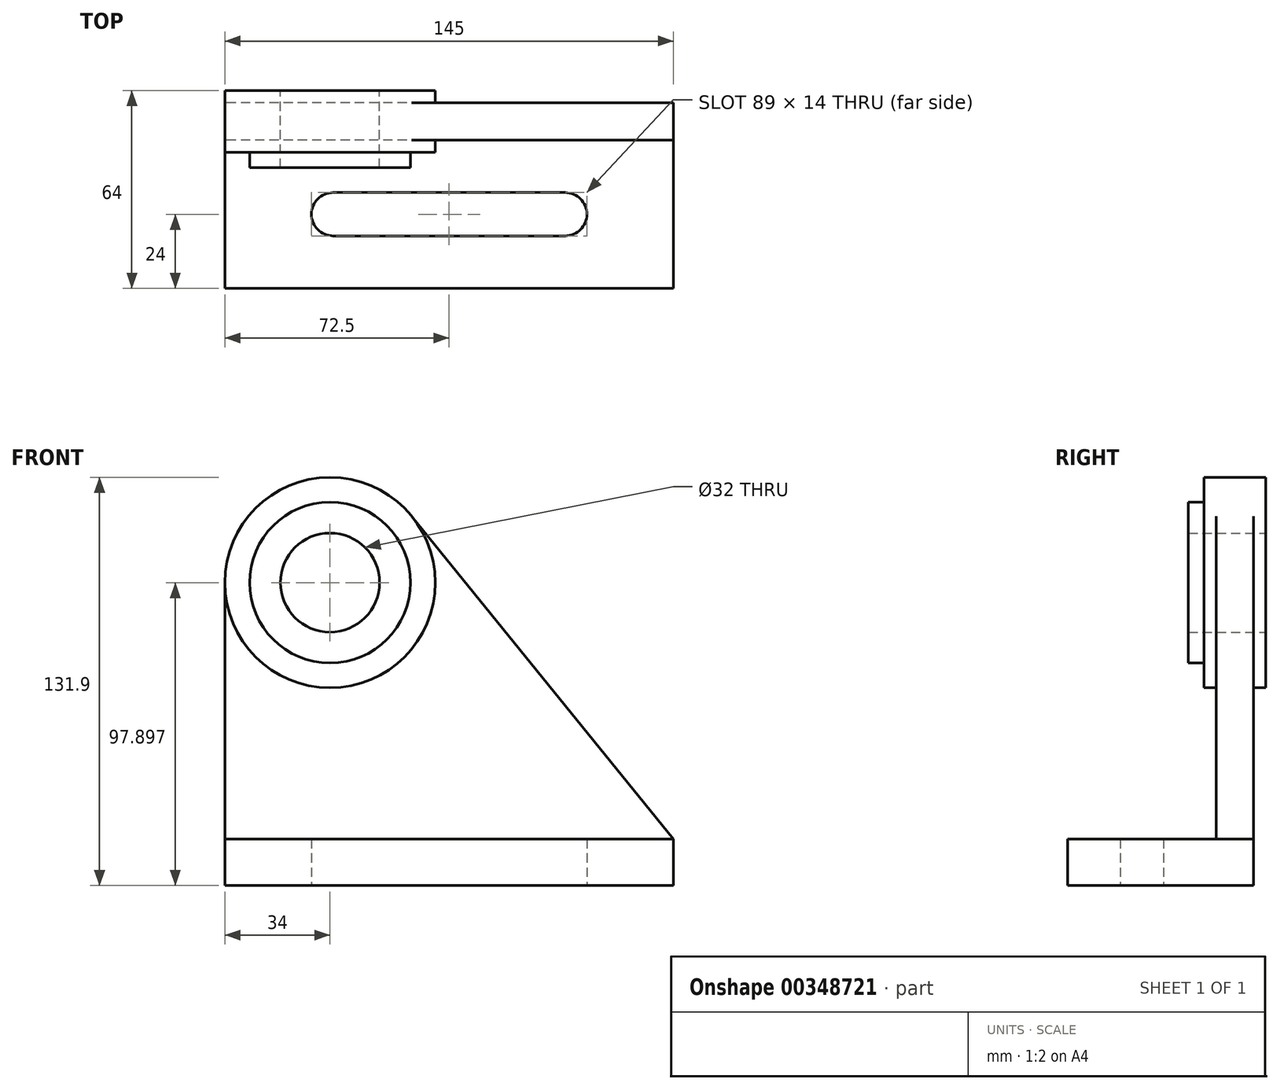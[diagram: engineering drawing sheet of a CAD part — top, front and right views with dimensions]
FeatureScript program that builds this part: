
annotation { "Feature Type Name" : "Feature", "Feature Type Description" : "" }
export const myFeature = defineFeature(function(context is Context, id is Id, definition is map)
    precondition{}
    {
        {
            var Q0;
            Q0=qCreatedBy(makeId("Top.planeOp"),FACE);
            var sketch = newSketch(context, id + "F0", { "sketchPlane" : qUnion([Q0])});
            skLineSegment(sketch, "E0.bottom", {"start": v(-72.5, 30) * mm, "end": v(72.5, 30) * mm});
            skLineSegment(sketch, "E0.top", {"start": v(-72.5, -30) * mm, "end": v(72.5, -30) * mm});
            skLineSegment(sketch, "E0.left", {"start": v(-72.5, 30) * mm, "end": v(-72.5, -30) * mm});
            skLineSegment(sketch, "E0.right", {"start": v(72.5, 30) * mm, "end": v(72.5, -30) * mm});
            skArc(sketch, "E1", {"start": v(37.5, -13) * mm, "mid": v(44.5, -6) * mm, "end": v(37.5, 1) * mm});
            skArc(sketch, "E2", {"start": v(-37.5, 1) * mm, "mid": v(-44.5, -6) * mm, "end": v(-37.5, -13) * mm});
            skLineSegment(sketch, "E3", {"start": v(-37.5, 1) * mm, "end": v(37.5, 1) * mm});
            skLineSegment(sketch, "E4", {"start": v(-37.5, -13) * mm, "end": v(37.5, -13) * mm});
            skSolve(sketch);
        }
        {
            var Q0;
            Q0 = qSketchRegion(id + "F0", true);
            extrude(context, id + "F1", {"entities" : qUnion([Q0]), "depth" : 15 * mm});
        }
        {
            var Q0;
            Q0=makeQuery(id+"F1.opExtrude","SWEPT_FACE",FACE,{"disambiguationData":[OSD([sQuery(id+"F0.wireOp",EDGE,"E0.bottom")])]});
            cPlane(context, id + "F2", {"entities" : qUnion([Q0]), "cplaneType" : CPlaneType.OFFSET, "offset" : 0 * mm, "width" : 150 * mm, "height" : 150 * mm});
        }
        {
            var Q0;
            Q0=qCreatedBy(id+"F2.planeOp",FACE);
            var sketch = newSketch(context, id + "F3", { "sketchPlane" : qUnion([Q0])});
            skLineSegment(sketch, "E5.bottom", {"start": v(-72.5, 15) * mm, "end": v(72.5, 15) * mm});
            skLineSegment(sketch, "E5.top", {"start": v(-72.5, 0) * mm, "end": v(72.5, 0) * mm});
            skLineSegment(sketch, "E5.left", {"start": v(-72.5, 15) * mm, "end": v(-72.5, 0) * mm});
            skLineSegment(sketch, "E5.right", {"start": v(72.5, 15) * mm, "end": v(72.5, 0) * mm});
            skLineSegment(sketch, "E6", {"start": v(72.5, 15) * mm, "end": v(72.5, 103.43) * mm});
            skCircle(sketch, "E7", {"center": v(38.5, 97.9) * mm, "radius": 16 * mm});
            skCircle(sketch, "E8", {"center": v(38.5, 97.9) * mm, "radius": 26 * mm});
            skCircle(sketch, "E9", {"center": v(38.5, 97.9) * mm, "radius": 34 * mm});
            skLineSegment(sketch, "E10", {"start": v(-72.5, 15) * mm, "end": v(12.1, 119.31) * mm});
            skSolve(sketch);
        }
        {
            var Q0;
            {var subQ0=sQuery(id+"F3.wireOp",EDGE,"E5.bottom");Q0=makeQuery(id+"F3.imprint","IMPRINT",FACE,{"disambiguationData":[TD([[makeQuery(id+"F3.imprint","IMPRINT",EDGE,{"derivedFrom":subQ0}),1.0]])]});}
            extrude(context, id + "F4", {"entities" : qUnion([Q0]), "operationType" : NewBodyOperationType.ADD, "oppositeDirection" : true, "depth" : 12 * mm});
        }
        {
            var Q0;
            Q0=makeQuery(id+"F3.imprint","IMPRINT",FACE,{"disambiguationData":[TD([[makeQuery(id+"F3.imprint","IMPRINT",EDGE,{"derivedFrom":sQuery(id+"F3.wireOp",EDGE,"E8")}),-1.0]])]});
            extrude(context, id + "F5", {"entities" : qUnion([Q0]), "operationType" : NewBodyOperationType.ADD, "oppositeDirection" : true, "depth" : 16 * mm});
        }
        {
            var Q0;
            Q0=makeQuery(id+"F3.imprint","IMPRINT",FACE,{"disambiguationData":[TD([[makeQuery(id+"F3.imprint","IMPRINT",EDGE,{"derivedFrom":sQuery(id+"F3.wireOp",EDGE,"E7")}),-1.0]])]});
            extrude(context, id + "F6", {"entities" : qUnion([Q0]), "operationType" : NewBodyOperationType.ADD, "oppositeDirection" : true, "depth" : 21 * mm});
        }
        {
            var Q0;
            Q0=makeQuery(id+"F3.imprint","IMPRINT",FACE,{"disambiguationData":[TD([[makeQuery(id+"F3.imprint","IMPRINT",EDGE,{"derivedFrom":sQuery(id+"F3.wireOp",EDGE,"E8")}),-1.0]])]});
            extrude(context, id + "F7", {"entities" : qUnion([Q0]), "operationType" : NewBodyOperationType.ADD, "depth" : 4 * mm});
        }
        {
            var Q0;
            Q0=makeQuery(id+"F3.imprint","IMPRINT",FACE,{"disambiguationData":[TD([[makeQuery(id+"F3.imprint","IMPRINT",EDGE,{"derivedFrom":sQuery(id+"F3.wireOp",EDGE,"E7")}),-1.0]])]});
            extrude(context, id + "F8", {"entities" : qUnion([Q0]), "operationType" : NewBodyOperationType.ADD, "depth" : 4 * mm});
        }
    });
